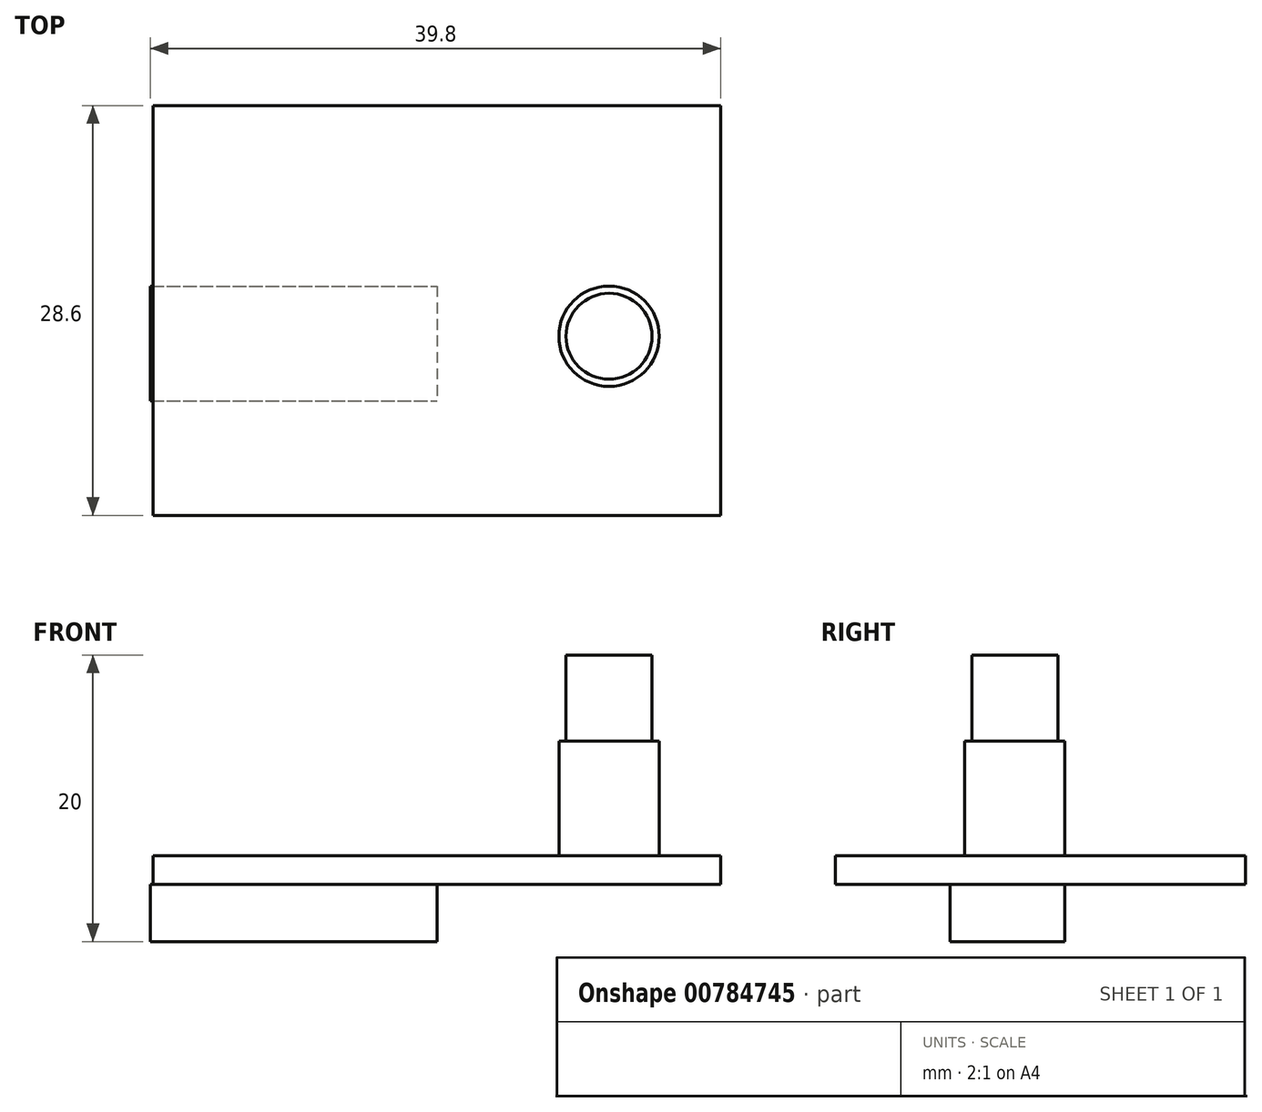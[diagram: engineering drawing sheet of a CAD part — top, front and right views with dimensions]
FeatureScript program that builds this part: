
annotation { "Feature Type Name" : "Feature", "Feature Type Description" : "" }
export const myFeature = defineFeature(function(context is Context, id is Id, definition is map)
    precondition{}
    {
        {
            var Q0;
            Q0=qCreatedBy(makeId("Top.planeOp"),FACE);
            var sketch = newSketch(context, id + "F0", { "sketchPlane" : qUnion([Q0])});
            skLineSegment(sketch, "E0.bottom", {"start": v(-19.8, 14.3) * mm, "end": v(19.8, 14.3) * mm});
            skLineSegment(sketch, "E0.top", {"start": v(-19.8, -14.3) * mm, "end": v(19.8, -14.3) * mm});
            skLineSegment(sketch, "E0.left", {"start": v(-19.8, 14.3) * mm, "end": v(-19.8, -14.3) * mm});
            skLineSegment(sketch, "E0.right", {"start": v(19.8, 14.3) * mm, "end": v(19.8, -14.3) * mm});
            skSolve(sketch);
        }
        {
            var Q0;
            Q0 = qSketchRegion(id + "F0", true);
            extrude(context, id + "F1", {"entities" : qUnion([Q0]), "depth" : 2 * mm, "offsetDistance" : 25 * mm});
        }
        {
            var Q0;
            Q0=qCreatedBy(makeId("Right.planeOp"),FACE);
            var sketch = newSketch(context, id + "F2", { "sketchPlane" : qUnion([Q0])});
            skLineSegment(sketch, "E1.bottom", {"start": v(1.7, 0) * mm, "end": v(-6.3, 0) * mm});
            skLineSegment(sketch, "E1.top", {"start": v(1.7, -4) * mm, "end": v(-6.3, -4) * mm});
            skLineSegment(sketch, "E1.left", {"start": v(1.7, 0) * mm, "end": v(1.7, -4) * mm});
            skLineSegment(sketch, "E1.right", {"start": v(-6.3, 0) * mm, "end": v(-6.3, -4) * mm});
            skSolve(sketch);
        }
        {
            var Q0;
            Q0 = qSketchRegion(id + "F2", true);
            extrude(context, id + "F3", {"entities" : qUnion([Q0]), "operationType" : NewBodyOperationType.ADD, "oppositeDirection" : true, "depth" : 20 * mm, "offsetDistance" : 25 * mm});
        }
        {
            var Q0;
            Q0=makeQuery(id+"F1.opExtrude","CAP_FACE",FACE,{"disambiguationData":[OSD([sQuery(id+"F0.wireOp",EDGE,"E0.bottom"),sQuery(id+"F0.wireOp",EDGE,"E0.top"),sQuery(id+"F0.wireOp",EDGE,"E0.left"),sQuery(id+"F0.wireOp",EDGE,"E0.right")])],"isStart":false});
            var sketch = newSketch(context, id + "F4", { "sketchPlane" : qUnion([Q0])});
            skCircle(sketch, "E2", {"center": v(12, -1.8) * mm, "radius": 3.5 * mm});
            skSolve(sketch);
        }
        {
            var Q0;
            Q0=makeQuery(id+"F4.imprint","IMPRINT",FACE,{"disambiguationData":[TD([[makeQuery(id+"F4.imprint","IMPRINT",EDGE,{"derivedFrom":sQuery(id+"F4.wireOp",EDGE,"E2")}),1.0]])]});
            extrude(context, id + "F5", {"entities" : qUnion([Q0]), "operationType" : NewBodyOperationType.ADD, "depth" : 8 * mm, "offsetDistance" : 25 * mm});
        }
        {
            var Q0;
            Q0=makeQuery(id+"F5.opExtrude","CAP_FACE",FACE,{"disambiguationData":[OSD([sQuery(id+"F4.wireOp",EDGE,"E2")])],"isStart":false});
            var sketch = newSketch(context, id + "F6", { "sketchPlane" : qUnion([Q0])});
            skCircle(sketch, "E3", {"center": v(12, -1.8) * mm, "radius": 3 * mm});
            skSolve(sketch);
        }
        {
            var Q0;
            Q0=makeQuery(id+"F6.imprint","IMPRINT",FACE,{"disambiguationData":[TD([[makeQuery(id+"F6.imprint","IMPRINT",EDGE,{"derivedFrom":sQuery(id+"F6.wireOp",EDGE,"E3")}),1.0]])]});
            extrude(context, id + "F7", {"entities" : qUnion([Q0]), "operationType" : NewBodyOperationType.ADD, "depth" : 6 * mm, "offsetDistance" : 25 * mm});
        }
    });
